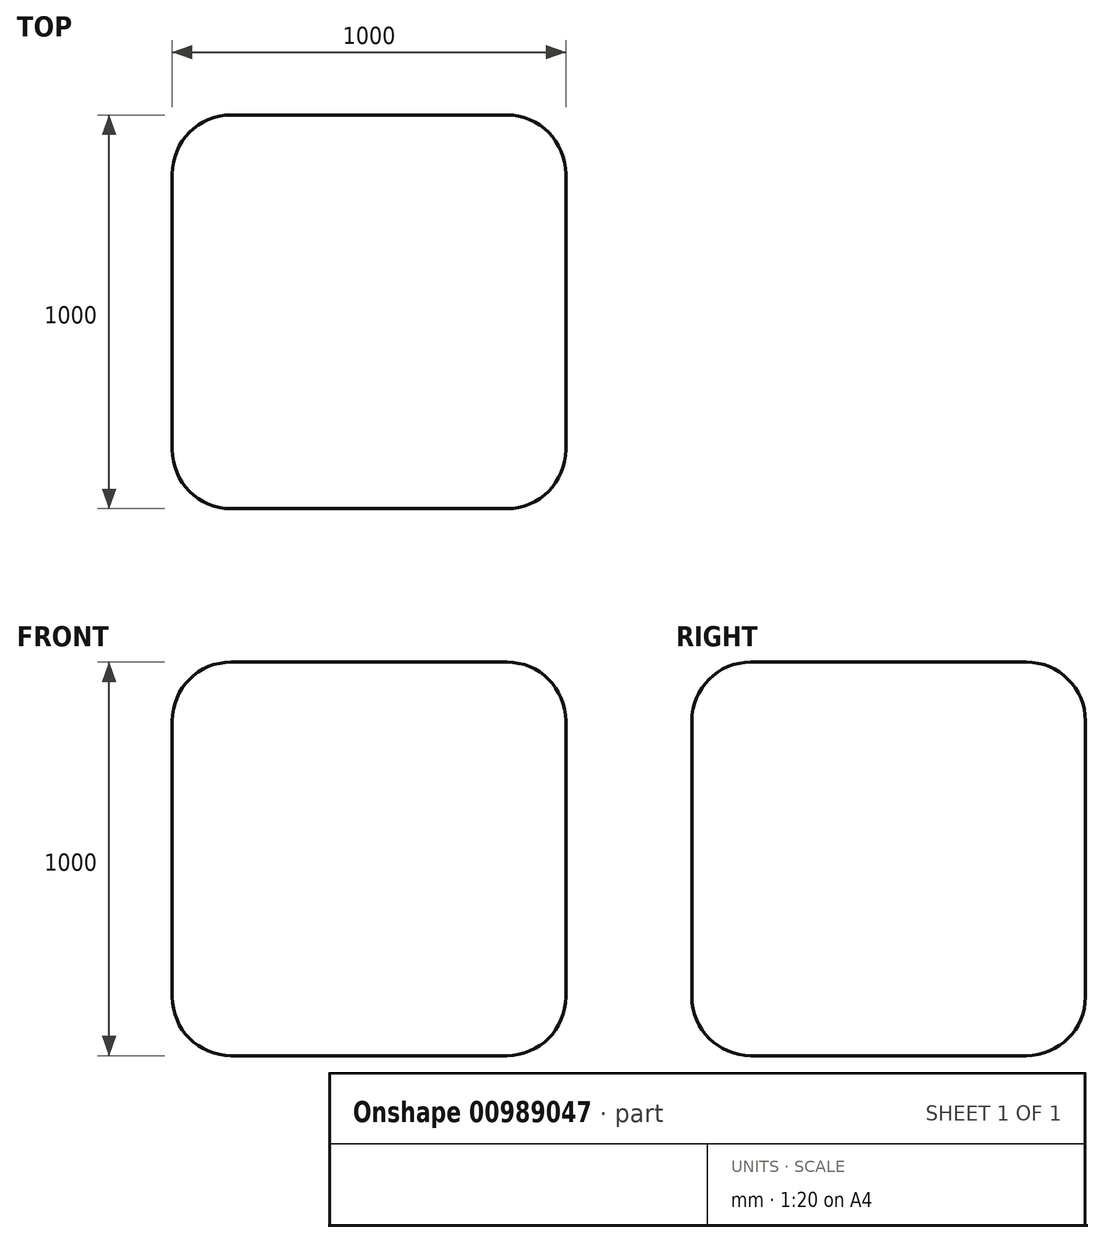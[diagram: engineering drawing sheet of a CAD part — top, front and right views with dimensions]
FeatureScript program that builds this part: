
annotation { "Feature Type Name" : "Feature", "Feature Type Description" : "" }
export const myFeature = defineFeature(function(context is Context, id is Id, definition is map)
    precondition{}
    {
        {
            var Q0;
            Q0=qCreatedBy(makeId("Top.planeOp"),FACE);
            var sketch = newSketch(context, id + "F0", { "sketchPlane" : qUnion([Q0])});
            skLineSegment(sketch, "E0.bottom", {"start": v(0, 0) * mm, "end": v(1000, 0) * mm});
            skLineSegment(sketch, "E0.top", {"start": v(0, 1000) * mm, "end": v(1000, 1000) * mm});
            skLineSegment(sketch, "E0.left", {"start": v(0, 0) * mm, "end": v(0, 1000) * mm});
            skLineSegment(sketch, "E0.right", {"start": v(1000, 0) * mm, "end": v(1000, 1000) * mm});
            skSolve(sketch);
        }
        {
            var Q0;
            Q0=makeQuery(id+"F0.imprint","IMPRINT",FACE,{"disambiguationData":[TD([[makeQuery(id+"F0.imprint","IMPRINT",EDGE,{"derivedFrom":sQuery(id+"F0.wireOp",EDGE,"E0.bottom")}),1.0]])]});
            extrude(context, id + "F1", {"entities" : qUnion([Q0]), "depth" : 1000 * mm, "offsetDistance" : 25 * mm});
        }
        {
            var Q0;
            Q0=makeQuery(id+"F1.opExtrude","CAP_EDGE",EDGE,{"disambiguationData":[OSD([sQuery(id+"F0.wireOp",EDGE,"E0.bottom")])],"isStart":false});
            var Q1;
            Q1=makeQuery(id+"F1.opExtrude","CAP_EDGE",EDGE,{"disambiguationData":[OSD([sQuery(id+"F0.wireOp",EDGE,"E0.left")])],"isStart":false});
            var Q2;
            Q2=makeQuery(id+"F1.opExtrude","CAP_EDGE",EDGE,{"disambiguationData":[OSD([sQuery(id+"F0.wireOp",EDGE,"E0.top")])],"isStart":false});
            var Q3;
            Q3=makeQuery(id+"F1.opExtrude","CAP_EDGE",EDGE,{"disambiguationData":[OSD([sQuery(id+"F0.wireOp",EDGE,"E0.right")])],"isStart":false});
            var Q4;
            Q4=makeQuery(id+"F1.opExtrude","CAP_EDGE",EDGE,{"disambiguationData":[OSD([sQuery(id+"F0.wireOp",EDGE,"E0.bottom")])],"isStart":true});
            var Q5;
            Q5=makeQuery(id+"F1.opExtrude","CAP_EDGE",EDGE,{"disambiguationData":[OSD([sQuery(id+"F0.wireOp",EDGE,"E0.left")])],"isStart":true});
            var Q6;
            Q6=makeQuery(id+"F1.opExtrude","CAP_EDGE",EDGE,{"disambiguationData":[OSD([sQuery(id+"F0.wireOp",EDGE,"E0.top")])],"isStart":true});
            var Q7;
            Q7=makeQuery(id+"F1.opExtrude","CAP_EDGE",EDGE,{"disambiguationData":[OSD([sQuery(id+"F0.wireOp",EDGE,"E0.right")])],"isStart":true});
            var Q8;
            Q8=makeQuery(id+"F1.opExtrude","SWEPT_FACE",FACE,{"disambiguationData":[OSD([sQuery(id+"F0.wireOp",EDGE,"E0.top")])]});
            var Q9;
            Q9=makeQuery(id+"F1.opExtrude","SWEPT_EDGE",EDGE,{"disambiguationData":[OSD([sQuery(id+"F0.wireOp",EDGE,"E0.bottom"),sQuery(id+"F0.wireOp",EDGE,"E0.right")])]});
            var Q10;
            Q10=makeQuery(id+"F1.opExtrude","SWEPT_EDGE",EDGE,{"disambiguationData":[OSD([sQuery(id+"F0.wireOp",EDGE,"E0.bottom"),sQuery(id+"F0.wireOp",EDGE,"E0.left")])]});
            fillet(context, id + "F2", {"entities" : qUnion([Q0, Q1, Q2, Q3, Q4, Q5, Q6, Q7, Q8, Q9, Q10]), "radius" : 150 * mm, "allowEdgeOverflow" : false});
        }
    });
